# Revit family: EU_EHS_ODU_UB1
name_source: partatom
category: Mechanical Equipment
revit_build: Autodesk Revit 2015 (Build: 20140606_1530(x64)
units: mm (PartAtom-declared; Revit-internal decimal feet)

## types (7) — shared parameters
Fan Grill Height = 653.88 mm
Fan Grill Length = 580.00 mm
Free Content Downloads = -
Location = -
Manufacturer = SAMSUNG
Manufacturer Metadata = -
Notes = -
Product Documentation Link = -
Product Page URL = -
Refrigerant Type = R410A
Sales Rep Locator = -
Serial Number = -
Subscribe for Update Alerts = -
System Served = -
URL = www.samsung.com

## per-type parameters (varying)
| type | Model | Net Weight |
| 9.00 kW, 220-240V, HEAT PUMP, SPLIT | AE090JXEDEH/EU | 68.00 kg |
| 9.00 kW, 380-415V, HEAT PUMP, SPLIT | AE090JXEDGH/EU | 76.00 kg |
| 9.00 kW, 220-240V, HEAT PUMP, MONO | AE090JXYDEH/EU | 76.00 kg |
| 9.00 kW, 380-415V, HEAT PUMP, MONO | AE090JXYDEH/EU | 76.00 kg |
| 6.60 kW, 220-240V, HEAT PUMP, TDM PLUS | AE066MXTPEH/EU | 61.00 kg |
| 9.00 kW, 220-240V, HEAT PUMP, TDM PLUS | AE090MXTPEH/EU | 74.00 kg |
| 9.00 kW, 380-415V, HEAT PUMP, TDM PLUS | AE090MXTPGH/EU | 76.00 kg |

## geometry (parser evidence)
native form markers: Sweep x18
no freeform markers — native parametric forms only
